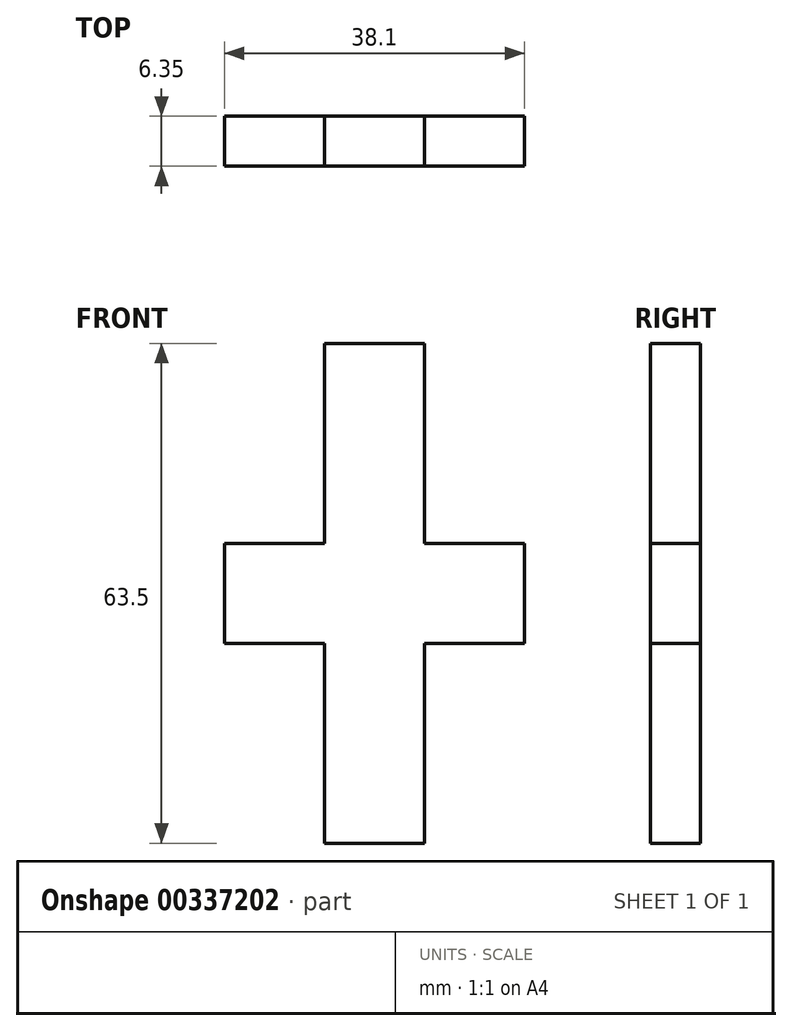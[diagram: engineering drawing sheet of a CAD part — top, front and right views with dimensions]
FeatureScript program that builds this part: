
annotation { "Feature Type Name" : "Feature", "Feature Type Description" : "" }
export const myFeature = defineFeature(function(context is Context, id is Id, definition is map)
    precondition{}
    {
        {
            var Q0;
            Q0=qCreatedBy(makeId("Front.planeOp"),FACE);
            var sketch = newSketch(context, id + "F0", { "sketchPlane" : qUnion([Q0])});
            skLineSegment(sketch, "E0", {"start": v(0, 0) * mm, "end": v(0, 25.4) * mm});
            skLineSegment(sketch, "E1", {"start": v(0, 25.4) * mm, "end": v(12.7, 25.4) * mm});
            skLineSegment(sketch, "E2", {"start": v(12.7, 25.4) * mm, "end": v(12.7, 0) * mm});
            skLineSegment(sketch, "E3", {"start": v(12.7, 0) * mm, "end": v(25.4, 0) * mm});
            skLineSegment(sketch, "E4", {"start": v(25.4, 0) * mm, "end": v(25.4, -12.7) * mm});
            skLineSegment(sketch, "E5", {"start": v(25.4, -12.7) * mm, "end": v(12.7, -12.7) * mm});
            skLineSegment(sketch, "E6", {"start": v(12.7, -12.7) * mm, "end": v(12.7, -38.1) * mm});
            skLineSegment(sketch, "E7", {"start": v(12.7, -38.1) * mm, "end": v(0, -38.1) * mm});
            skLineSegment(sketch, "E8", {"start": v(0, -38.1) * mm, "end": v(0, -12.7) * mm});
            skLineSegment(sketch, "E9", {"start": v(0, -12.7) * mm, "end": v(-12.7, -12.7) * mm});
            skLineSegment(sketch, "E10", {"start": v(-12.7, -12.7) * mm, "end": v(-12.7, 0) * mm});
            skLineSegment(sketch, "E11", {"start": v(0, 0) * mm, "end": v(-12.7, 0) * mm});
            skSolve(sketch);
        }
        {
            var Q0;
            Q0=makeQuery(id+"F0.imprint","IMPRINT",FACE,{"disambiguationData":[TD([[makeQuery(id+"F0.imprint","IMPRINT",EDGE,{"derivedFrom":sQuery(id+"F0.wireOp",EDGE,"E0")}),-1.0]])]});
            extrude(context, id + "F1", {"entities" : qUnion([Q0]), "depth" : 6.35 * mm});
        }
    });
